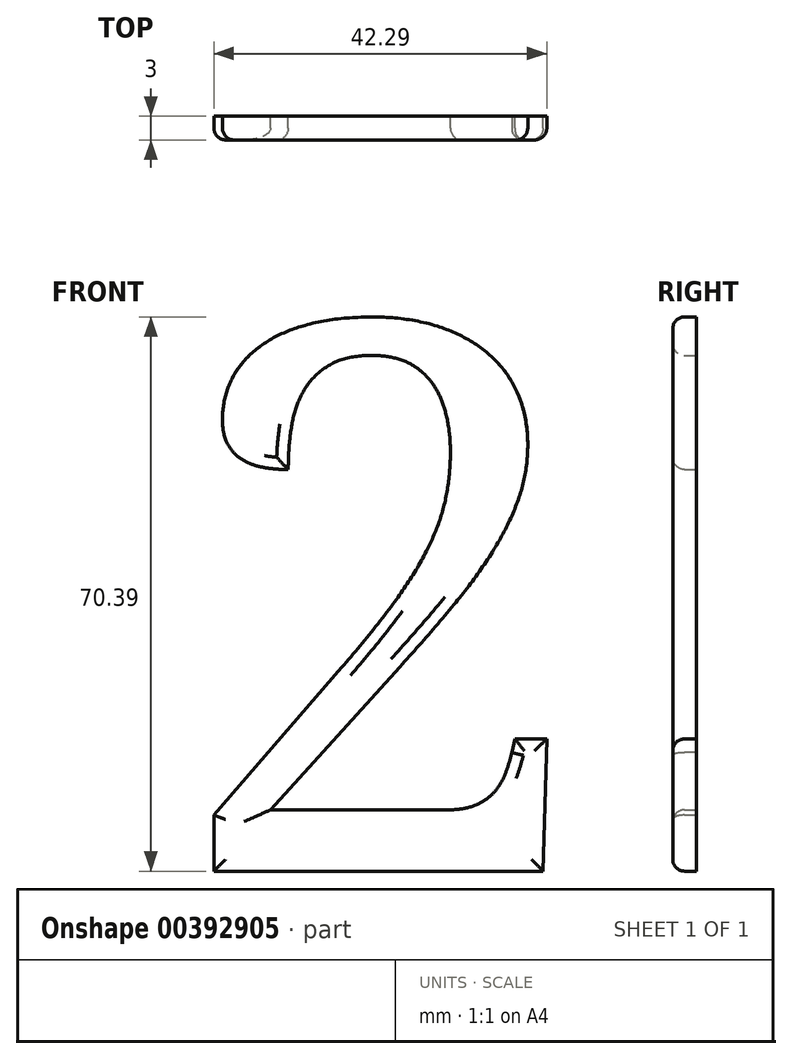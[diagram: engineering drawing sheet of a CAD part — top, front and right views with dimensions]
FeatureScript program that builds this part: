
annotation { "Feature Type Name" : "Feature", "Feature Type Description" : "" }
export const myFeature = defineFeature(function(context is Context, id is Id, definition is map)
    precondition{}
    {
        {
            var Q0;
            Q0=qCreatedBy(makeId("Front.planeOp"),FACE);
            var sketch = newSketch(context, id + "F0", { "sketchPlane" : qUnion([Q0])});
            skText(sketch, "E0", { "text": "2", "fontName": "NotoSerif-Regular.ttf"});
            const initialGuessF0  = {"E0": [0.00494, 0, 1, 0, 0.07]};
            skSetInitialGuess(sketch, initialGuessF0);
            skSolve(sketch);
        }
        {
            var Q0;
            Q0 = qSketchRegion(id + "F0", true);
            extrude(context, id + "F1", {"entities" : qUnion([Q0]), "depth" : 3 * mm});
        }
        {
            var Q0;
            Q0=makeQuery(id+"F1.opExtrude","CAP_FACE",FACE,{"disambiguationData":[OSD([sQuery(id+"F0.wireOp",EDGE,"E0.sketch_text.stroke-0"),sQuery(id+"F0.wireOp",EDGE,"E0.sketch_text.stroke-1"),sQuery(id+"F0.wireOp",EDGE,"E0.sketch_text.stroke-2"),sQuery(id+"F0.wireOp",EDGE,"E0.sketch_text.stroke-3"),sQuery(id+"F0.wireOp",EDGE,"E0.sketch_text.stroke-4"),sQuery(id+"F0.wireOp",EDGE,"E0.sketch_text.stroke-5"),sQuery(id+"F0.wireOp",EDGE,"E0.sketch_text.stroke-6"),sQuery(id+"F0.wireOp",EDGE,"E0.sketch_text.stroke-7"),sQuery(id+"F0.wireOp",EDGE,"E0.sketch_text.stroke-8"),sQuery(id+"F0.wireOp",EDGE,"E0.sketch_text.stroke-9"),sQuery(id+"F0.wireOp",EDGE,"E0.sketch_text.stroke-10"),sQuery(id+"F0.wireOp",EDGE,"E0.sketch_text.stroke-11"),sQuery(id+"F0.wireOp",EDGE,"E0.sketch_text.stroke-12"),sQuery(id+"F0.wireOp",EDGE,"E0.sketch_text.stroke-13"),sQuery(id+"F0.wireOp",EDGE,"E0.sketch_text.stroke-14"),sQuery(id+"F0.wireOp",EDGE,"E0.sketch_text.stroke-15"),sQuery(id+"F0.wireOp",EDGE,"E0.sketch_text.stroke-16"),sQuery(id+"F0.wireOp",EDGE,"E0.sketch_text.stroke-17"),sQuery(id+"F0.wireOp",EDGE,"E0.sketch_text.stroke-18"),sQuery(id+"F0.wireOp",EDGE,"E0.sketch_text.stroke-19"),sQuery(id+"F0.wireOp",EDGE,"E0.sketch_text.stroke-20"),sQuery(id+"F0.wireOp",EDGE,"E0.sketch_text.stroke-21"),sQuery(id+"F0.wireOp",EDGE,"E0.sketch_text.stroke-22"),sQuery(id+"F0.wireOp",EDGE,"E0.sketch_text.stroke-23"),sQuery(id+"F0.wireOp",EDGE,"E0.sketch_text.stroke-24"),sQuery(id+"F0.wireOp",EDGE,"E0.sketch_text.stroke-25"),sQuery(id+"F0.wireOp",EDGE,"E0.sketch_text.stroke-26"),sQuery(id+"F0.wireOp",EDGE,"E0.sketch_text.stroke-27"),sQuery(id+"F0.wireOp",EDGE,"E0.sketch_text.stroke-28"),sQuery(id+"F0.wireOp",EDGE,"E0.sketch_text.stroke-29"),sQuery(id+"F0.wireOp",EDGE,"E0.sketch_text.stroke-30"),sQuery(id+"F0.wireOp",EDGE,"E0.sketch_text.stroke-31"),sQuery(id+"F0.wireOp",EDGE,"E0.sketch_text.stroke-32"),sQuery(id+"F0.wireOp",EDGE,"E0.sketch_text.stroke-33"),sQuery(id+"F0.wireOp",EDGE,"E0.sketch_text.stroke-34"),sQuery(id+"F0.wireOp",EDGE,"E0.sketch_text.stroke-35"),sQuery(id+"F0.wireOp",EDGE,"E0.sketch_text.stroke-36"),sQuery(id+"F0.wireOp",EDGE,"E0.sketch_text.stroke-37"),sQuery(id+"F0.wireOp",EDGE,"E0.sketch_text.stroke-38"),sQuery(id+"F0.wireOp",EDGE,"E0.sketch_text.stroke-39")])],"isStart":false});
            fillet(context, id + "F2", {"entities" : qUnion([Q0]), "radius" : 1.5 * mm, "tangentPropagation" : true, "allowEdgeOverflow" : false});
        }
    });
